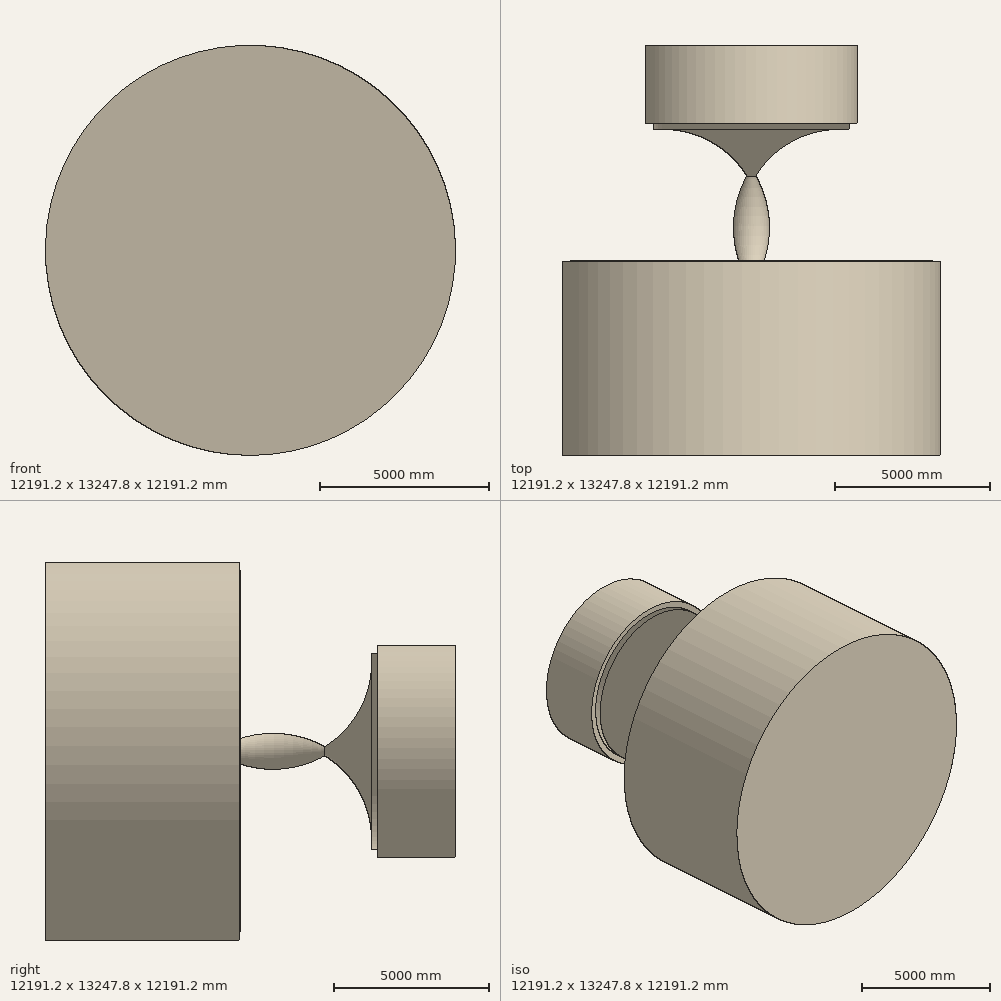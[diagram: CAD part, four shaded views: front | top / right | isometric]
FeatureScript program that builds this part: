
annotation { "Feature Type Name" : "Feature", "Feature Type Description" : "" }
export const myFeature = defineFeature(function(context is Context, id is Id, definition is map)
    precondition{}
    {
        {
            var Q0;
            Q0=qCreatedBy(makeId("Top.planeOp"),FACE);
            var sketch = newSketch(context, id + "F0", { "sketchPlane" : qUnion([Q0])});
            skLineSegment(sketch, "E0", {"start": v(0, 0) * mm, "end": v(0, 16091.55) * mm, "construction": true});
            skLineSegment(sketch, "E1", {"start": v(3414.47, 13247.8) * mm, "end": v(3414.47, 10741.52) * mm});
            skArc(sketch, "E2", {"start": v(6095.6, 6253.56) * mm, "mid": v(5792.61, 9117.4) * mm, "end": v(3414.47, 10741.52) * mm});
            skLineSegment(sketch, "E3", {"start": v(6095.6, 6253.56) * mm, "end": v(6095.6, 0) * mm});
            skLineSegment(sketch, "E4", {"start": v(0, 0) * mm, "end": v(6095.6, 0) * mm});
            skLineSegment(sketch, "E5", {"start": v(0, 0) * mm, "end": v(0, 13247.8) * mm});
            skLineSegment(sketch, "E6", {"start": v(0, 13247.8) * mm, "end": v(3414.47, 13247.8) * mm});
            skSolve(sketch);
        }
        {
            var Q0;
            Q0 = qSketchRegion(id + "F0", true);
            var Q1;
            Q1=sQuery(id+"F0.wireOp",EDGE,"E0");
            revolve(context, id + "F1", {"entities" : qUnion([Q0]), "axis" : qUnion([Q1]), "revolveType" : RevolveType.FULL});
        }
        {
            var Q0;
            Q0=makeQuery(id+"F1.opRevolve","SWEPT_FACE",FACE,{"disambiguationData":[OSD([sQuery(id+"F0.wireOp",EDGE,"E6")])]});
            shell(context, id + "F2", {"entities" : qUnion([Q0]), "thickness" : 254 * mm});
        }
    });
